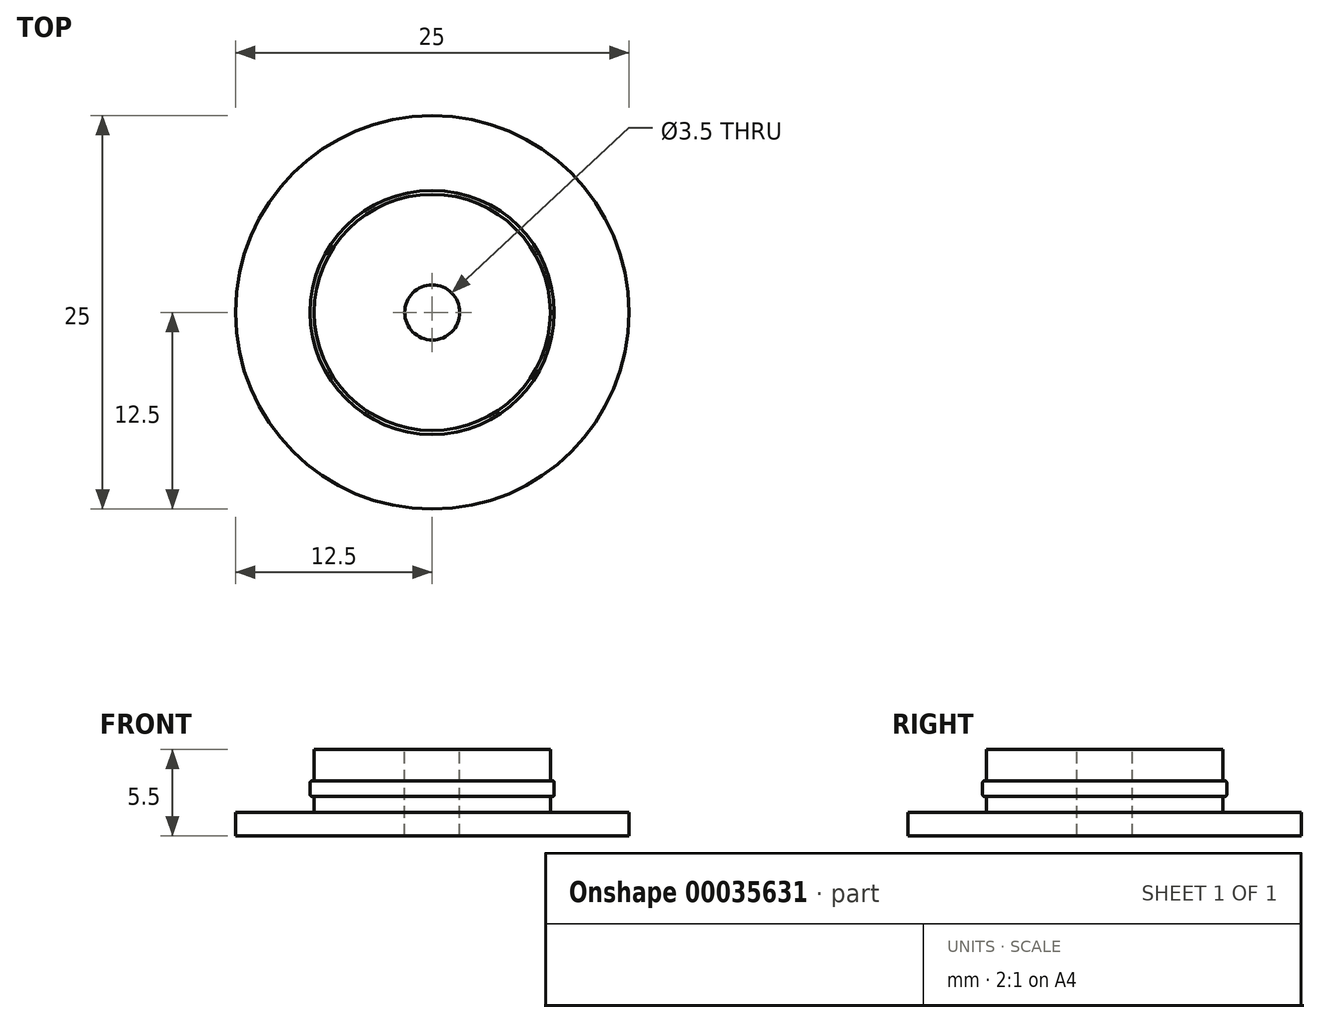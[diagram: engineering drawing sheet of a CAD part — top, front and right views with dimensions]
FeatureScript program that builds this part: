
annotation { "Feature Type Name" : "Feature", "Feature Type Description" : "" }
export const myFeature = defineFeature(function(context is Context, id is Id, definition is map)
    precondition{}
    {
        {
            var Q0;
            Q0=qCreatedBy(makeId("Top.planeOp"),FACE);
            var sketch = newSketch(context, id + "F0", { "sketchPlane" : qUnion([Q0])});
            skCircle(sketch, "E0", {"center": v(0, 0) * mm, "radius": 12.5 * mm});
            skSolve(sketch);
        }
        {
            var Q0;
            Q0 = qSketchRegion(id + "F0", true);
            extrude(context, id + "F1", {"entities" : qUnion([Q0]), "depth" : 1.5 * mm});
        }
        {
            var Q0;
            Q0=makeQuery(id+"F1.opExtrude","CAP_FACE",FACE,{"disambiguationData":[OSD([sQuery(id+"F0.wireOp",EDGE,"E0")])],"isStart":false});
            var sketch = newSketch(context, id + "F2", { "sketchPlane" : qUnion([Q0])});
            skCircle(sketch, "E1", {"center": v(0, 0) * mm, "radius": 7.5 * mm});
            skSolve(sketch);
        }
        {
            var Q0;
            Q0 = qSketchRegion(id + "F2", true);
            extrude(context, id + "F3", {"entities" : qUnion([Q0]), "operationType" : NewBodyOperationType.ADD, "depth" : 1 * mm});
        }
        {
            var Q0;
            Q0=makeQuery(id+"F3.opExtrude","CAP_FACE",FACE,{"disambiguationData":[OSD([sQuery(id+"F2.wireOp",EDGE,"E1")])],"isStart":false});
            var sketch = newSketch(context, id + "F4", { "sketchPlane" : qUnion([Q0])});
            skCircle(sketch, "E2", {"center": v(0, 0) * mm, "radius": 7.75 * mm});
            skSolve(sketch);
        }
        {
            var Q0;
            Q0 = qSketchRegion(id + "F4", true);
            extrude(context, id + "F5", {"entities" : qUnion([Q0]), "operationType" : NewBodyOperationType.ADD, "depth" : 1 * mm});
        }
        {
            var Q0;
            Q0=makeQuery(id+"F5.opExtrude","CAP_FACE",FACE,{"disambiguationData":[OSD([sQuery(id+"F4.wireOp",EDGE,"E2")])],"isStart":false});
            var sketch = newSketch(context, id + "F6", { "sketchPlane" : qUnion([Q0])});
            skCircle(sketch, "E3", {"center": v(0, 0) * mm, "radius": 7.5 * mm});
            skSolve(sketch);
        }
        {
            var Q0;
            Q0=makeQuery(id+"F6.imprint","IMPRINT",FACE,{"disambiguationData":[TD([[makeQuery(id+"F6.imprint","IMPRINT",EDGE,{"derivedFrom":sQuery(id+"F6.wireOp",EDGE,"E3")}),1.0]])]});
            extrude(context, id + "F7", {"entities" : qUnion([Q0]), "operationType" : NewBodyOperationType.ADD, "depth" : 2 * mm});
        }
        {
            var Q0;
            Q0=makeQuery(id+"F7.opExtrude","CAP_FACE",FACE,{"disambiguationData":[OSD([sQuery(id+"F6.wireOp",EDGE,"E3")])],"isStart":false});
            var sketch = newSketch(context, id + "F8", { "sketchPlane" : qUnion([Q0])});
            skSolve(sketch);
        }
        {
            var Q0;
            Q0=makeQuery(id+"F8.imprint","IMPRINT",FACE,{"disambiguationData":[TD([[makeQuery(id+"F8.imprint","IMPRINT",EDGE,{"derivedFrom":makeQuery(id+"F7.opExtrude","CAP_EDGE",EDGE,{"disambiguationData":[OSD([sQuery(id+"F6.wireOp",EDGE,"E3")])],"isStart":false})}),1.0]])]});
            var sketch = newSketch(context, id + "F9", { "sketchPlane" : qUnion([Q0])});
            skCircle(sketch, "E4", {"center": v(0, 0) * mm, "radius": 1.75 * mm});
            skSolve(sketch);
        }
        {
            var Q0;
            Q0=makeQuery(id+"F9.imprint","IMPRINT",FACE,{"disambiguationData":[TD([[makeQuery(id+"F9.imprint","IMPRINT",EDGE,{"derivedFrom":sQuery(id+"F9.wireOp",EDGE,"E4")}),1.0]])]});
            extrude(context, id + "F10", {"entities" : qUnion([Q0]), "operationType" : NewBodyOperationType.REMOVE, "endBound" : BoundingType.THROUGH_ALL, "oppositeDirection" : true, "depth" : 25.4 * mm});
        }
        {
            var Q0;
            Q0=makeQuery(id+"F5.opExtrude","CAP_EDGE",EDGE,{"disambiguationData":[OSD([sQuery(id+"F4.wireOp",EDGE,"E2")])],"isStart":false});
            var Q1;
            Q1=makeQuery(id+"F5.opExtrude","CAP_EDGE",EDGE,{"disambiguationData":[OSD([sQuery(id+"F4.wireOp",EDGE,"E2")])],"isStart":true});
            fillet(context, id + "F11", {"entities" : qUnion([Q0, Q1]), "radius" : .125 * mm, "tangentPropagation" : true, "allowEdgeOverflow" : false});
        }
    });
